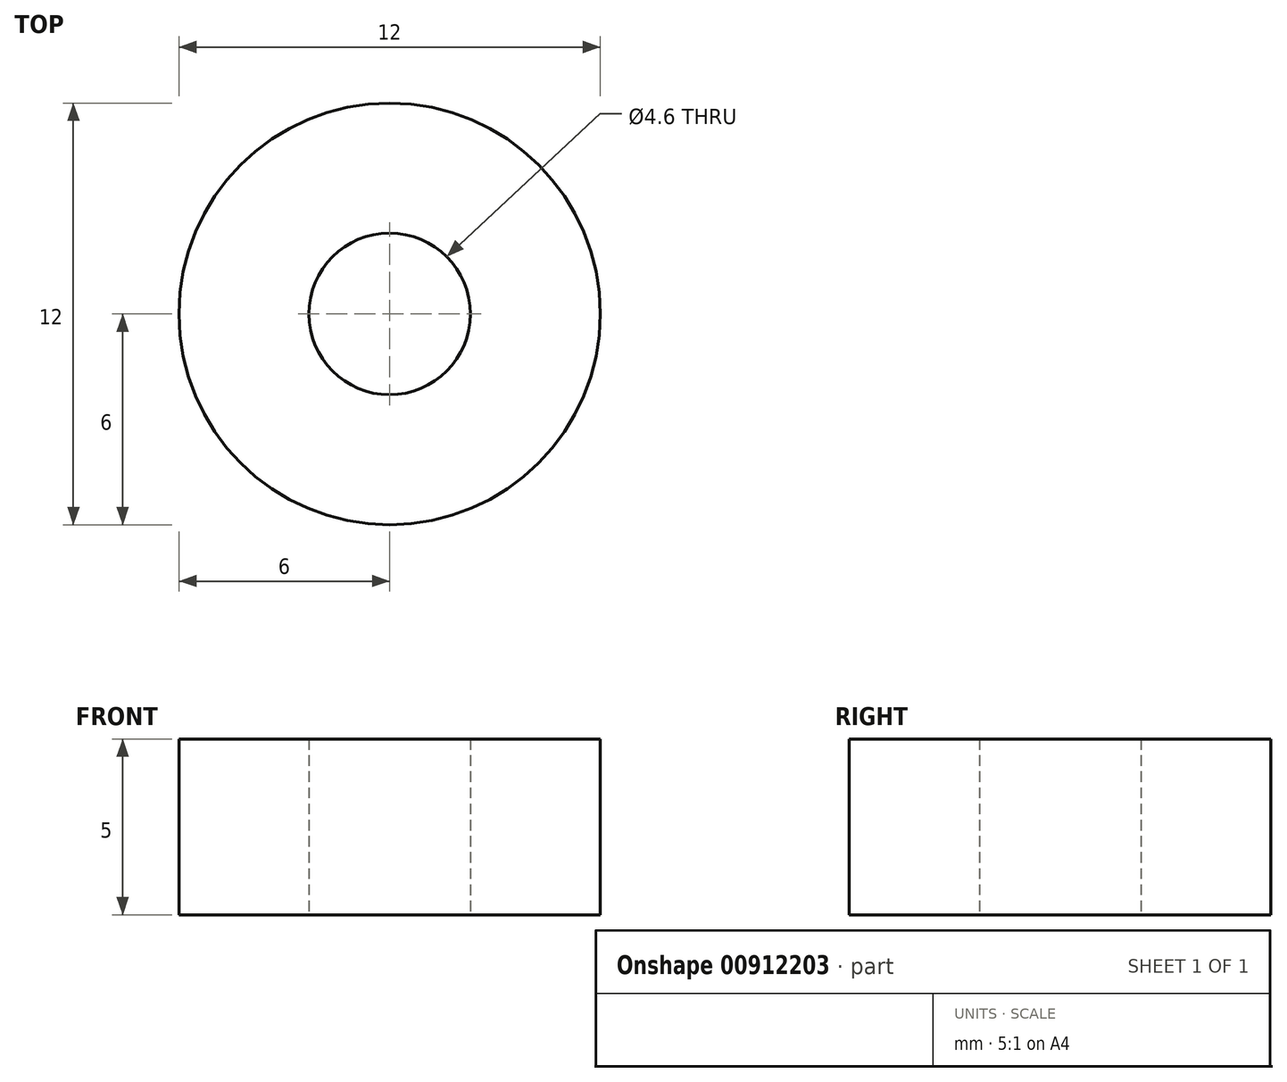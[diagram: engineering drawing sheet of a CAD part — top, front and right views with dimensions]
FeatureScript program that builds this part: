
annotation { "Feature Type Name" : "Feature", "Feature Type Description" : "" }
export const myFeature = defineFeature(function(context is Context, id is Id, definition is map)
    precondition{}
    {
        {
            var Q0;
            Q0=qCreatedBy(makeId("Top.planeOp"),FACE);
            var sketch = newSketch(context, id + "F0", { "sketchPlane" : qUnion([Q0])});
            skCircle(sketch, "E0", {"center": v(0, 0) * mm, "radius": 2.3 * mm});
            skCircle(sketch, "E1", {"center": v(0, 0) * mm, "radius": 6 * mm});
            skSolve(sketch);
        }
        {
            var Q0;
            Q0=makeQuery(id+"F0.imprint","IMPRINT",FACE,{"disambiguationData":[TD([[makeQuery(id+"F0.imprint","IMPRINT",EDGE,{"derivedFrom":sQuery(id+"F0.wireOp",EDGE,"E0")}),-1.0]])]});
            extrude(context, id + "F1", {"entities" : qUnion([Q0]), "depth" : 5 * mm, "offsetDistance" : 25 * mm});
        }
    });
